# Revit family: TR3003
name_source: partatom
category: Verbindungsmittel
units: mm (PartAtom-declared; Revit-internal decimal feet)

## family parameters
Arbeitsebenenbasiert = Nein
Beim Laden mit Abzugskörper schneiden = Nein
Gemeinsam genutzt = Nein
Immer vertikal = Nein
OmniClass-Nummer = 23.25.10.27.11.21
OmniClass-Titel = Reinforcement Couplers

## types (10) — shared parameters
Endenbearbeitung 1 = Mit Gewinde
Endenbearbeitung 2 = Mit Gewinde
Hersteller = Stahlwerk Annahütte Max Aicher GmbH Co.KG
Modell = TR 3003
TR3003-G_Vis = Ja
TR3003-L_Vis = Ja
Typenbild = TR3003.png
Typenkommentare = TR 3003 - Standardmuffe
URL = http//:www.annahuette.com

## per-type parameters (varying)
| type | Außendurchmesser | Beschreibung | Einfassung Stab 1 | Einfassung Stab 2 | Gesamtlänge | Körper | Stabgröße 1 | Stabgröße 2 | TR3003-G | TR3003-L | TR3003-ø | TR3003-ød |
| TR 3003-ø18 | 36 mm  [stored 0.11811 ft] | TR3003-ø18 | 50 mm  [stored 0.164042 ft] | 50 mm  [stored 0.164042 ft] | 100 mm  [stored 0.328084 ft] | 0,57 kg | SAS 670 - ø18 | SAS 670 - ø18 | 0,57 kg | 100 mm  [stored 0.328084 ft] | 36 mm  [stored 0.11811 ft] | 18 mm  [stored 0.0590551 ft] |
| TR 3003-ø22 | 40 mm  [stored 0.131234 ft] | TR3003-ø22 | 55 mm  [stored 0.180446 ft] | 55 mm  [stored 0.180446 ft] | 110 mm  [stored 0.360892 ft] | 0,55 kg | SAS 670 - ø22 | SAS 670 - ø22 | 0,55 kg | 110 mm  [stored 0.360892 ft] | 40 mm  [stored 0.131234 ft] | 22 mm  [stored 0.0721785 ft] |
| TR 3003-ø25 | 45 mm  [stored 0.147638 ft] | TR3003-ø25 | 65 mm  [stored 0.213255 ft] | 65 mm  [stored 0.213255 ft] | 130 mm  [stored 0.426509 ft] | 1,05 kg | SAS 670 - ø25 | SAS 670 - ø25 | 1,05 kg | 130 mm  [stored 0.426509 ft] | 45 mm  [stored 0.147638 ft] | 25 mm  [stored 0.082021 ft] |
| TR 3003-ø28 | 50 mm  [stored 0.164042 ft] | TR3003-ø28 | 70 mm  [stored 0.229659 ft] | 70 mm  [stored 0.229659 ft] | 140 mm  [stored 0.459318 ft] | 1,36 kg | SAS 670 - ø28 | SAS 670 - ø28 | 1,36 kg | 140 mm  [stored 0.459318 ft] | 50 mm  [stored 0.164042 ft] | 28 mm  [stored 0.0918635 ft] |
| TR 3003-ø30 | 55 mm  [stored 0.180446 ft] | TR3003-ø30 | 75 mm | 75 mm | 150 mm | 1,84 kg | SAS 670 - ø30 | SAS 670 - ø30 | 1,84 kg | 150 mm | 55 mm  [stored 0.180446 ft] | 30 mm  [stored 0.0984252 ft] |
| TR 3003-ø35 | 65 mm  [stored 0.213255 ft] | TR3003-ø35 | 90 mm  [stored 0.295276 ft] | 90 mm  [stored 0.295276 ft] | 180 mm  [stored 0.590551 ft] | 3,16 kg | SAS 670 - ø35 | SAS 670 - ø35 | 3,16 kg | 180 mm  [stored 0.590551 ft] | 65 mm  [stored 0.213255 ft] | 35 mm  [stored 0.114829 ft] |
| TR 3003-ø43 | 80 mm  [stored 0.262467 ft] | TR3003-ø43 | 100 mm  [stored 0.328084 ft] | 100 mm  [stored 0.328084 ft] | 200 mm  [stored 0.656168 ft] | 5,42 kg | SAS 670 - ø43 | SAS 670 - ø43 | 5,42 kg | 200 mm  [stored 0.656168 ft] | 80 mm  [stored 0.262467 ft] | 43 mm  [stored 0.141076 ft] |
| TR 3003-ø50 | 90 mm  [stored 0.295276 ft] | TR3003-ø50 | 105 mm  [stored 0.344488 ft] | 105 mm  [stored 0.344488 ft] | 210 mm  [stored 0.688976 ft] | 6,92 kg | SAS 670 - ø50 | SAS 670 - ø50 | 6,92 kg | 210 mm  [stored 0.688976 ft] | 90 mm  [stored 0.295276 ft] | 50 mm  [stored 0.164042 ft] |
| TR 3003-ø57,5 | 102 mm | TR3003-ø57,5 | 125 mm  [stored 0.410105 ft] | 125 mm  [stored 0.410105 ft] | 250 mm  [stored 0.82021 ft] | 10,37 kg | SAS 670 - ø57,5 | SAS 670 - ø57,5 | 10,37 kg | 250 mm  [stored 0.82021 ft] | 102 mm | 58 mm |
| TR 3003-ø63,5 | 114 mm  [stored 0.374016 ft] | TR3003-ø63,5 | 150 mm | 150 mm | 300 mm | 15,85 kg | SAS 670 - ø63,5 | SAS 670 - ø63,5 | 15,85 kg | 300 mm | 114 mm  [stored 0.374016 ft] | 64 mm |

note: [stored X ft] marks values corroborated as IEEE doubles in the binary element streams (Revit-internal decimal feet)
